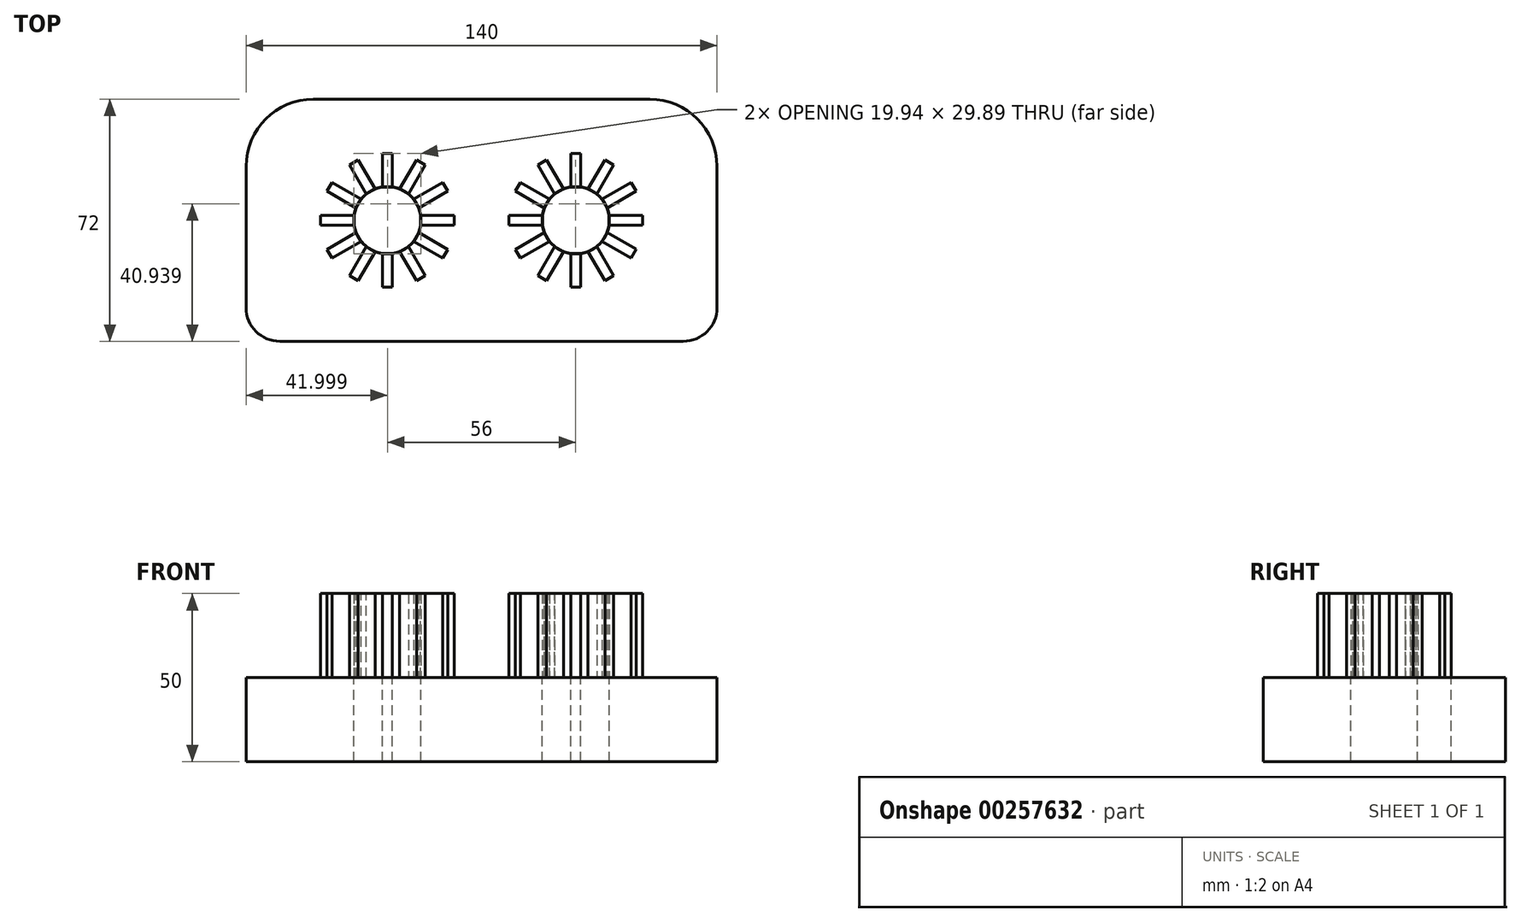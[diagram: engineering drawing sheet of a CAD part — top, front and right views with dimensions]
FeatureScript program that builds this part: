
annotation { "Feature Type Name" : "Feature", "Feature Type Description" : "" }
export const myFeature = defineFeature(function(context is Context, id is Id, definition is map)
    precondition{}
    {
        {
            var Q0;
            Q0=qCreatedBy(makeId("Top.planeOp"),FACE);
            var sketch = newSketch(context, id + "F0", { "sketchPlane" : qUnion([Q0])});
            skLineSegment(sketch, "E0", {"start": v(-61.23, -12.32) * mm, "end": v(-29.23, -12.32) * mm});
            skLineSegment(sketch, "E1", {"start": v(-29.23, -12.32) * mm, "end": v(26.77, -12.32) * mm});
            skLineSegment(sketch, "E2", {"start": v(26.77, -12.32) * mm, "end": v(58.77, -12.32) * mm});
            skLineSegment(sketch, "E3", {"start": v(68.77, -2.32) * mm, "end": v(68.77, 23.68) * mm});
            skLineSegment(sketch, "E4", {"start": v(68.77, 23.68) * mm, "end": v(68.77, 39.68) * mm});
            skLineSegment(sketch, "E5", {"start": v(48.77, 59.68) * mm, "end": v(-51.23, 59.68) * mm});
            skLineSegment(sketch, "E6", {"start": v(-71.23, 39.68) * mm, "end": v(-71.23, -2.32) * mm});
            skPoint(sketch, "E7.visualSharp", {"position": v(-71.23, 59.68) * mm});
            skArc(sketch, "E7.filletArc", {"start": v(-51.23, 59.68) * mm, "mid": v(-65.37, 53.82) * mm, "end": v(-71.23, 39.68) * mm});
            skPoint(sketch, "E8.visualSharp", {"position": v(68.77, 59.68) * mm});
            skArc(sketch, "E8.filletArc", {"start": v(68.77, 39.68) * mm, "mid": v(62.91, 53.82) * mm, "end": v(48.77, 59.68) * mm});
            skPoint(sketch, "E9.visualSharp", {"position": v(-71.23, -12.32) * mm});
            skArc(sketch, "E9.filletArc", {"start": v(-71.23, -2.32) * mm, "mid": v(-68.3, -9.4) * mm, "end": v(-61.23, -12.32) * mm});
            skPoint(sketch, "E10.visualSharp", {"position": v(68.77, -12.32) * mm});
            skArc(sketch, "E10.filletArc", {"start": v(58.77, -12.32) * mm, "mid": v(65.84, -9.4) * mm, "end": v(68.77, -2.32) * mm});
            skPoint(sketch, "E11", {"position": v(26.77, 23.68) * mm});
            skPoint(sketch, "E12", {"position": v(-29.23, 23.68) * mm});
            skCircle(sketch, "E13", {"center": v(-29.23, 23.68) * mm, "radius": 10 * mm});
            skCircle(sketch, "E14", {"center": v(26.77, 23.68) * mm, "radius": 10 * mm});
            skLineSegment(sketch, "E15", {"start": v(26.77, 33.56) * mm, "end": v(26.77, 33.68) * mm});
            skPoint(sketch, "E16", {"position": v(-30.73, 33.68) * mm});
            skPoint(sketch, "E17", {"position": v(-27.73, 33.68) * mm});
            skPoint(sketch, "E18", {"position": v(-30.73, 33.56) * mm});
            skPoint(sketch, "E19", {"position": v(-27.73, 33.56) * mm});
            skLineSegment(sketch, "E20.top", {"start": v(-30.73, 43.56) * mm, "end": v(-27.73, 43.56) * mm});
            skLineSegment(sketch, "E20.left", {"start": v(-30.73, 33.56) * mm, "end": v(-30.73, 43.56) * mm});
            skLineSegment(sketch, "E20.right", {"start": v(-27.73, 33.56) * mm, "end": v(-27.73, 43.56) * mm});
            skPoint(sketch, "E21.center", {"position": v(0, 0) * mm});
            skPoint(sketch, "E22", {"position": v(28.26, 33.68) * mm});
            skPoint(sketch, "E23", {"position": v(25.27, 33.68) * mm});
            skPoint(sketch, "E24", {"position": v(25.26, 33.56) * mm});
            skPoint(sketch, "E25", {"position": v(28.26, 33.56) * mm});
            skLineSegment(sketch, "E26.top", {"start": v(25.26, 43.56) * mm, "end": v(28.26, 43.56) * mm});
            skLineSegment(sketch, "E26.left", {"start": v(25.26, 33.56) * mm, "end": v(25.26, 43.56) * mm});
            skLineSegment(sketch, "E26.right", {"start": v(28.26, 33.56) * mm, "end": v(28.26, 43.56) * mm});
            skLineSegment(sketch, "E27", {"start": v(-27.73, 33.56) * mm, "end": v(-30.73, 33.56) * mm});
            skLineSegment(sketch, "E28", {"start": v(28.26, 33.56) * mm, "end": v(25.26, 33.56) * mm});
            skSolve(sketch);
        }
        {
            var Q0;
            {var subQ0=sQuery(id+"F0.wireOp",EDGE,"E27");Q0=makeQuery(id+"F0.imprint","IMPRINT",FACE,{"disambiguationData":[TD([[makeQuery(id+"F0.imprint","IMPRINT",EDGE,{"derivedFrom":subQ0}),1.0]])]});}
            var Q1;
            Q1=makeQuery(id+"F0.imprint","IMPRINT",FACE,{"disambiguationData":[TD([[makeQuery(id+"F0.imprint","IMPRINT",EDGE,{"derivedFrom":sQuery(id+"F0.wireOp",EDGE,"E20.top")}),-1.0]])]});
            var Q2;
            {var subQ0=sQuery(id+"F0.wireOp",EDGE,"E28");var subQ4=makeQuery(id+"F0.imprint","INTERSECT",VERTEX,{"derivedFrom":[sQuery(id+"F0.wireOp",EDGE,"E15"),subQ0]});Q2=makeQuery(id+"F0.imprint","IMPRINT",FACE,{"disambiguationData":[TD([[makeQuery(id+"F0.imprint","IMPRINT",EDGE,{"disambiguationData":[TD([[subQ4,1.0]])],"derivedFrom":subQ0}),1.0]])]});}
            var Q3;
            {var subQ1=sQuery(id+"F0.wireOp",EDGE,"E26.top");Q3=makeQuery(id+"F0.imprint","IMPRINT",FACE,{"disambiguationData":[TD([[makeQuery(id+"F0.imprint","IMPRINT",EDGE,{"derivedFrom":subQ1}),-1.0]])]});}
            extrude(context, id + "F1", {"entities" : qUnion([Q0, Q1, Q2, Q3]), "depth" : 25 * mm});
        }
        {
            var Q0;
            Q0=makeQuery(id+"F1.opExtrude","SWEPT_BODY",BODY,{"disambiguationData":[OSD([sQuery(id+"F0.wireOp",EDGE,"E13"),sQuery(id+"F0.wireOp",EDGE,"E20.top"),sQuery(id+"F0.wireOp",EDGE,"E20.left"),sQuery(id+"F0.wireOp",EDGE,"E20.right")])]});
            var Q1;
            Q1=makeQuery(id+"F1.opExtrude","SWEPT_BODY",BODY,{"disambiguationData":[OSD([sQuery(id+"F0.wireOp",EDGE,"E13"),sQuery(id+"F0.wireOp",EDGE,"E27")])]});
            var Q2;
            {var subQ0=sQuery(id+"F0.wireOp",EDGE,"E27");var subQ1=sQuery(id+"F0.wireOp",EDGE,"E13");Q2=makeQuery(id+"F1.opExtrude","SWEPT_FACE",FACE,{"disambiguationData":[OSD([subQ1]),TDD([makeQuery(id+"F0.imprint","IMPRINT",EDGE,{"disambiguationData":[TD([[makeQuery(id+"F0.imprint","INTERSECT",VERTEX,{"derivedFrom":[subQ1,sQuery(id+"F0.wireOp",EDGE,"E20.left"),subQ0]}),-1.0]])],"derivedFrom":subQ1})])]});}
            circularPattern(context, id + "F2", {"entities" : qUnion([Q0, Q1]), "axis" : qUnion([Q2]), "angle" : 360 * degree, "instanceCount" : 12, "equalSpace" : true});
        }
        {
            var Q0;
            Q0=makeQuery(id+"F1.opExtrude","SWEPT_BODY",BODY,{"disambiguationData":[OSD([sQuery(id+"F0.wireOp",EDGE,"E14"),sQuery(id+"F0.wireOp",EDGE,"E28")])]});
            var Q1;
            Q1=makeQuery(id+"F1.opExtrude","SWEPT_BODY",BODY,{"disambiguationData":[OSD([sQuery(id+"F0.wireOp",EDGE,"E14"),sQuery(id+"F0.wireOp",EDGE,"E26.top"),sQuery(id+"F0.wireOp",EDGE,"E26.left"),sQuery(id+"F0.wireOp",EDGE,"E26.right")])]});
            var Q2;
            {var subQ0=sQuery(id+"F0.wireOp",EDGE,"E28");var subQ1=sQuery(id+"F0.wireOp",EDGE,"E14");Q2=makeQuery(id+"F1.opExtrude","SWEPT_FACE",FACE,{"disambiguationData":[OSD([subQ1]),TDD([makeQuery(id+"F0.imprint","IMPRINT",EDGE,{"disambiguationData":[TD([[makeQuery(id+"F0.imprint","INTERSECT",VERTEX,{"derivedFrom":[subQ1,sQuery(id+"F0.wireOp",EDGE,"E26.left"),subQ0]}),-1.0]])],"derivedFrom":subQ1})])]});}
            circularPattern(context, id + "F3", {"entities" : qUnion([Q0, Q1]), "axis" : qUnion([Q2]), "angle" : 360 * degree, "instanceCount" : 12, "equalSpace" : true});
        }
        {
            var Q0;
            Q0 = qSketchRegion(id + "F0", true);
            var Q1;
            Q1=makeQuery(id+"F1.opExtrude","CAP_FACE",FACE,{"disambiguationData":[OSD([sQuery(id+"F0.wireOp",EDGE,"E13"),sQuery(id+"F0.wireOp",EDGE,"E20.top"),sQuery(id+"F0.wireOp",EDGE,"E20.left"),sQuery(id+"F0.wireOp",EDGE,"E20.right")])],"isStart":false});
            var Q2;
            Q2=makeQuery(id+"F2.opPattern","COPY",FACE,{"derivedFrom":makeQuery(id+"F1.opExtrude","CAP_FACE",FACE,{"disambiguationData":[OSD([sQuery(id+"F0.wireOp",EDGE,"E13"),sQuery(id+"F0.wireOp",EDGE,"E20.top"),sQuery(id+"F0.wireOp",EDGE,"E20.left"),sQuery(id+"F0.wireOp",EDGE,"E20.right")])],"isStart":false}),"instanceName":"11"});
            var Q3;
            Q3=makeQuery(id+"F2.opPattern","COPY",FACE,{"derivedFrom":makeQuery(id+"F1.opExtrude","CAP_FACE",FACE,{"disambiguationData":[OSD([sQuery(id+"F0.wireOp",EDGE,"E13"),sQuery(id+"F0.wireOp",EDGE,"E20.top"),sQuery(id+"F0.wireOp",EDGE,"E20.left"),sQuery(id+"F0.wireOp",EDGE,"E20.right")])],"isStart":false}),"instanceName":"10"});
            var Q4;
            Q4=makeQuery(id+"F2.opPattern","COPY",FACE,{"derivedFrom":makeQuery(id+"F1.opExtrude","CAP_FACE",FACE,{"disambiguationData":[OSD([sQuery(id+"F0.wireOp",EDGE,"E13"),sQuery(id+"F0.wireOp",EDGE,"E20.top"),sQuery(id+"F0.wireOp",EDGE,"E20.left"),sQuery(id+"F0.wireOp",EDGE,"E20.right")])],"isStart":false}),"instanceName":"9"});
            var Q5;
            Q5=makeQuery(id+"F2.opPattern","COPY",FACE,{"derivedFrom":makeQuery(id+"F1.opExtrude","CAP_FACE",FACE,{"disambiguationData":[OSD([sQuery(id+"F0.wireOp",EDGE,"E13"),sQuery(id+"F0.wireOp",EDGE,"E20.top"),sQuery(id+"F0.wireOp",EDGE,"E20.left"),sQuery(id+"F0.wireOp",EDGE,"E20.right")])],"isStart":false}),"instanceName":"8"});
            var Q6;
            Q6=makeQuery(id+"F2.opPattern","COPY",FACE,{"derivedFrom":makeQuery(id+"F1.opExtrude","CAP_FACE",FACE,{"disambiguationData":[OSD([sQuery(id+"F0.wireOp",EDGE,"E13"),sQuery(id+"F0.wireOp",EDGE,"E20.top"),sQuery(id+"F0.wireOp",EDGE,"E20.left"),sQuery(id+"F0.wireOp",EDGE,"E20.right")])],"isStart":false}),"instanceName":"7"});
            var Q7;
            Q7=makeQuery(id+"F2.opPattern","COPY",FACE,{"derivedFrom":makeQuery(id+"F1.opExtrude","CAP_FACE",FACE,{"disambiguationData":[OSD([sQuery(id+"F0.wireOp",EDGE,"E13"),sQuery(id+"F0.wireOp",EDGE,"E20.top"),sQuery(id+"F0.wireOp",EDGE,"E20.left"),sQuery(id+"F0.wireOp",EDGE,"E20.right")])],"isStart":false}),"instanceName":"6"});
            var Q8;
            Q8=makeQuery(id+"F2.opPattern","COPY",FACE,{"derivedFrom":makeQuery(id+"F1.opExtrude","CAP_FACE",FACE,{"disambiguationData":[OSD([sQuery(id+"F0.wireOp",EDGE,"E13"),sQuery(id+"F0.wireOp",EDGE,"E20.top"),sQuery(id+"F0.wireOp",EDGE,"E20.left"),sQuery(id+"F0.wireOp",EDGE,"E20.right")])],"isStart":false}),"instanceName":"5"});
            var Q9;
            Q9=makeQuery(id+"F2.opPattern","COPY",FACE,{"derivedFrom":makeQuery(id+"F1.opExtrude","CAP_FACE",FACE,{"disambiguationData":[OSD([sQuery(id+"F0.wireOp",EDGE,"E13"),sQuery(id+"F0.wireOp",EDGE,"E20.top"),sQuery(id+"F0.wireOp",EDGE,"E20.left"),sQuery(id+"F0.wireOp",EDGE,"E20.right")])],"isStart":false}),"instanceName":"4"});
            var Q10;
            Q10=makeQuery(id+"F2.opPattern","COPY",FACE,{"derivedFrom":makeQuery(id+"F1.opExtrude","CAP_FACE",FACE,{"disambiguationData":[OSD([sQuery(id+"F0.wireOp",EDGE,"E13"),sQuery(id+"F0.wireOp",EDGE,"E20.top"),sQuery(id+"F0.wireOp",EDGE,"E20.left"),sQuery(id+"F0.wireOp",EDGE,"E20.right")])],"isStart":false}),"instanceName":"3"});
            var Q11;
            Q11=makeQuery(id+"F2.opPattern","COPY",FACE,{"derivedFrom":makeQuery(id+"F1.opExtrude","CAP_FACE",FACE,{"disambiguationData":[OSD([sQuery(id+"F0.wireOp",EDGE,"E13"),sQuery(id+"F0.wireOp",EDGE,"E20.top"),sQuery(id+"F0.wireOp",EDGE,"E20.left"),sQuery(id+"F0.wireOp",EDGE,"E20.right")])],"isStart":false}),"instanceName":"2"});
            var Q12;
            Q12=makeQuery(id+"F2.opPattern","COPY",FACE,{"derivedFrom":makeQuery(id+"F1.opExtrude","CAP_FACE",FACE,{"disambiguationData":[OSD([sQuery(id+"F0.wireOp",EDGE,"E13"),sQuery(id+"F0.wireOp",EDGE,"E20.top"),sQuery(id+"F0.wireOp",EDGE,"E20.left"),sQuery(id+"F0.wireOp",EDGE,"E20.right")])],"isStart":false}),"instanceName":"1"});
            var Q13;
            Q13=makeQuery(id+"F1.opExtrude","CAP_FACE",FACE,{"disambiguationData":[OSD([sQuery(id+"F0.wireOp",EDGE,"E13"),sQuery(id+"F0.wireOp",EDGE,"E27")])],"isStart":false});
            var Q14;
            Q14=makeQuery(id+"F1.opExtrude","CAP_FACE",FACE,{"disambiguationData":[OSD([sQuery(id+"F0.wireOp",EDGE,"E14"),sQuery(id+"F0.wireOp",EDGE,"E28")])],"isStart":false});
            var Q15;
            Q15=makeQuery(id+"F1.opExtrude","CAP_FACE",FACE,{"disambiguationData":[OSD([sQuery(id+"F0.wireOp",EDGE,"E14"),sQuery(id+"F0.wireOp",EDGE,"E26.top"),sQuery(id+"F0.wireOp",EDGE,"E26.left"),sQuery(id+"F0.wireOp",EDGE,"E26.right")])],"isStart":false});
            var Q16;
            Q16=makeQuery(id+"F3.opPattern","COPY",FACE,{"derivedFrom":makeQuery(id+"F1.opExtrude","CAP_FACE",FACE,{"disambiguationData":[OSD([sQuery(id+"F0.wireOp",EDGE,"E14"),sQuery(id+"F0.wireOp",EDGE,"E26.top"),sQuery(id+"F0.wireOp",EDGE,"E26.left"),sQuery(id+"F0.wireOp",EDGE,"E26.right")])],"isStart":false}),"instanceName":"11"});
            var Q17;
            Q17=makeQuery(id+"F3.opPattern","COPY",FACE,{"derivedFrom":makeQuery(id+"F1.opExtrude","CAP_FACE",FACE,{"disambiguationData":[OSD([sQuery(id+"F0.wireOp",EDGE,"E14"),sQuery(id+"F0.wireOp",EDGE,"E26.top"),sQuery(id+"F0.wireOp",EDGE,"E26.left"),sQuery(id+"F0.wireOp",EDGE,"E26.right")])],"isStart":false}),"instanceName":"10"});
            var Q18;
            Q18=makeQuery(id+"F3.opPattern","COPY",FACE,{"derivedFrom":makeQuery(id+"F1.opExtrude","CAP_FACE",FACE,{"disambiguationData":[OSD([sQuery(id+"F0.wireOp",EDGE,"E14"),sQuery(id+"F0.wireOp",EDGE,"E26.top"),sQuery(id+"F0.wireOp",EDGE,"E26.left"),sQuery(id+"F0.wireOp",EDGE,"E26.right")])],"isStart":false}),"instanceName":"9"});
            var Q19;
            Q19=makeQuery(id+"F3.opPattern","COPY",FACE,{"derivedFrom":makeQuery(id+"F1.opExtrude","CAP_FACE",FACE,{"disambiguationData":[OSD([sQuery(id+"F0.wireOp",EDGE,"E14"),sQuery(id+"F0.wireOp",EDGE,"E26.top"),sQuery(id+"F0.wireOp",EDGE,"E26.left"),sQuery(id+"F0.wireOp",EDGE,"E26.right")])],"isStart":false}),"instanceName":"8"});
            var Q20;
            Q20=makeQuery(id+"F3.opPattern","COPY",FACE,{"derivedFrom":makeQuery(id+"F1.opExtrude","CAP_FACE",FACE,{"disambiguationData":[OSD([sQuery(id+"F0.wireOp",EDGE,"E14"),sQuery(id+"F0.wireOp",EDGE,"E26.top"),sQuery(id+"F0.wireOp",EDGE,"E26.left"),sQuery(id+"F0.wireOp",EDGE,"E26.right")])],"isStart":false}),"instanceName":"7"});
            var Q21;
            Q21=makeQuery(id+"F3.opPattern","COPY",FACE,{"derivedFrom":makeQuery(id+"F1.opExtrude","CAP_FACE",FACE,{"disambiguationData":[OSD([sQuery(id+"F0.wireOp",EDGE,"E14"),sQuery(id+"F0.wireOp",EDGE,"E26.top"),sQuery(id+"F0.wireOp",EDGE,"E26.left"),sQuery(id+"F0.wireOp",EDGE,"E26.right")])],"isStart":false}),"instanceName":"6"});
            var Q22;
            Q22=makeQuery(id+"F3.opPattern","COPY",FACE,{"derivedFrom":makeQuery(id+"F1.opExtrude","CAP_FACE",FACE,{"disambiguationData":[OSD([sQuery(id+"F0.wireOp",EDGE,"E14"),sQuery(id+"F0.wireOp",EDGE,"E26.top"),sQuery(id+"F0.wireOp",EDGE,"E26.left"),sQuery(id+"F0.wireOp",EDGE,"E26.right")])],"isStart":false}),"instanceName":"5"});
            var Q23;
            Q23=makeQuery(id+"F3.opPattern","COPY",FACE,{"derivedFrom":makeQuery(id+"F1.opExtrude","CAP_FACE",FACE,{"disambiguationData":[OSD([sQuery(id+"F0.wireOp",EDGE,"E14"),sQuery(id+"F0.wireOp",EDGE,"E26.top"),sQuery(id+"F0.wireOp",EDGE,"E26.left"),sQuery(id+"F0.wireOp",EDGE,"E26.right")])],"isStart":false}),"instanceName":"4"});
            var Q24;
            Q24=makeQuery(id+"F3.opPattern","COPY",FACE,{"derivedFrom":makeQuery(id+"F1.opExtrude","CAP_FACE",FACE,{"disambiguationData":[OSD([sQuery(id+"F0.wireOp",EDGE,"E14"),sQuery(id+"F0.wireOp",EDGE,"E26.top"),sQuery(id+"F0.wireOp",EDGE,"E26.left"),sQuery(id+"F0.wireOp",EDGE,"E26.right")])],"isStart":false}),"instanceName":"3"});
            var Q25;
            Q25=makeQuery(id+"F3.opPattern","COPY",FACE,{"derivedFrom":makeQuery(id+"F1.opExtrude","CAP_FACE",FACE,{"disambiguationData":[OSD([sQuery(id+"F0.wireOp",EDGE,"E14"),sQuery(id+"F0.wireOp",EDGE,"E26.top"),sQuery(id+"F0.wireOp",EDGE,"E26.left"),sQuery(id+"F0.wireOp",EDGE,"E26.right")])],"isStart":false}),"instanceName":"2"});
            var Q26;
            Q26=makeQuery(id+"F3.opPattern","COPY",FACE,{"derivedFrom":makeQuery(id+"F1.opExtrude","CAP_FACE",FACE,{"disambiguationData":[OSD([sQuery(id+"F0.wireOp",EDGE,"E14"),sQuery(id+"F0.wireOp",EDGE,"E26.top"),sQuery(id+"F0.wireOp",EDGE,"E26.left"),sQuery(id+"F0.wireOp",EDGE,"E26.right")])],"isStart":false}),"instanceName":"1"});
            extrude(context, id + "F4", {"entities" : qUnion([Q0, Q1, Q2, Q3, Q4, Q5, Q6, Q7, Q8, Q9, Q10, Q11, Q12, Q13, Q14, Q15, Q16, Q17, Q18, Q19, Q20, Q21, Q22, Q23, Q24, Q25, Q26]), "oppositeDirection" : true, "depth" : 25 * mm});
        }
    });
